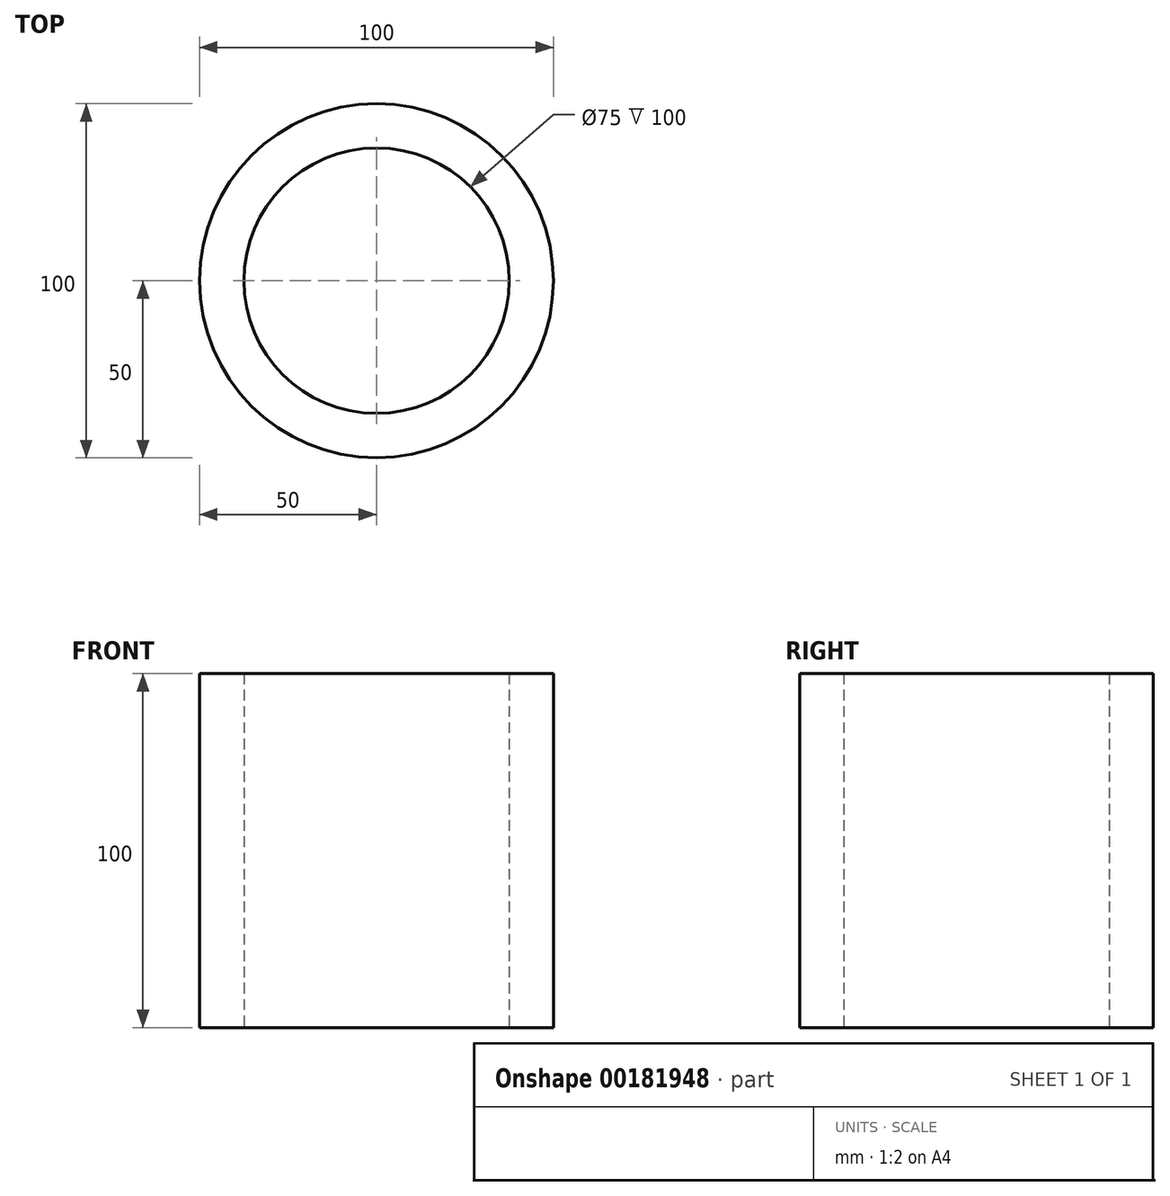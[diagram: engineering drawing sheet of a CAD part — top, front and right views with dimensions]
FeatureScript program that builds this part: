
annotation { "Feature Type Name" : "Feature", "Feature Type Description" : "" }
export const myFeature = defineFeature(function(context is Context, id is Id, definition is map)
    precondition{}
    {
        {
            var Q0;
            Q0=qCreatedBy(makeId("Top.planeOp"),FACE);
            var sketch = newSketch(context, id + "F0", { "sketchPlane" : qUnion([Q0])});
            skCircle(sketch, "E0", {"center": v(0, 0) * mm, "radius": 50 * mm});
            skCircle(sketch, "E1", {"center": v(0, 0) * mm, "radius": 37.5 * mm});
            skSolve(sketch);
        }
        {
            var Q0;
            Q0=makeQuery(id+"F0.imprint","IMPRINT",FACE,{"disambiguationData":[TD([[makeQuery(id+"F0.imprint","IMPRINT",EDGE,{"derivedFrom":sQuery(id+"F0.wireOp",EDGE,"E0")}),1.0]])]});
            extrude(context, id + "F1", {"entities" : qUnion([Q0]), "depth" : 100 * mm});
        }
    });
